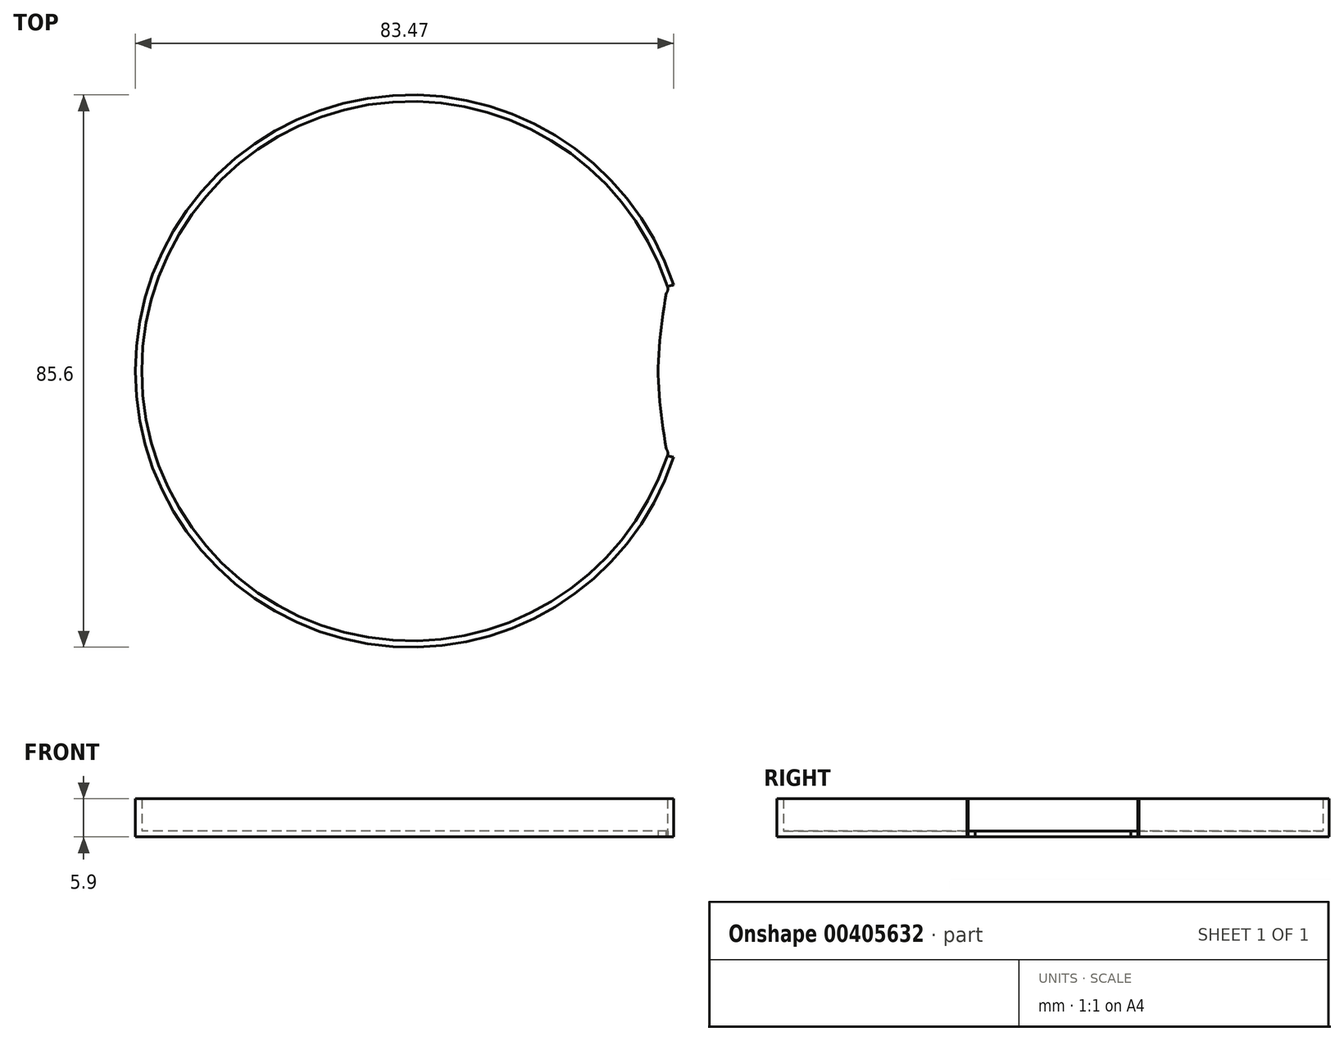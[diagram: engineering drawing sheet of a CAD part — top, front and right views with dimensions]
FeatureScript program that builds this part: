
annotation { "Feature Type Name" : "Feature", "Feature Type Description" : "" }
export const myFeature = defineFeature(function(context is Context, id is Id, definition is map)
    precondition{}
    {
        {
            var Q0;
            Q0=qCreatedBy(makeId("Top.planeOp"),FACE);
            var sketch = newSketch(context, id + "F0", { "sketchPlane" : qUnion([Q0])});
            skCircle(sketch, "E0", {"center": v(0, 0) * mm, "radius": 42.8 * mm});
            skCircle(sketch, "E1", {"center": v(42.8, 0) * mm, "radius": 13.5 * mm});
            skCircle(sketch, "E2.0", {"center": v(0, 0) * mm, "radius": 41.8 * mm});
            skCircle(sketch, "E3.0", {"center": v(42.8, 0) * mm, "radius": 12.5 * mm});
            skFitSpline(sketch, "E4", {"points": [v(39.68, -13.14) * mm, v(38.27, 0) * mm, v(39.68, 13.14) * mm], "startDerivative": vector(-4.24, 26.27) * mm, "endDerivative": vector(4.24, 26.27) * mm});
            skSolve(sketch);
        }
        {
            var Q0;
            {var subQ0=sQuery(id+"F0.wireOp",EDGE,"E2.0");var subQ1=sQuery(id+"F0.wireOp",EDGE,"E1");var subQ2=makeQuery(id+"F0.imprint","INTERSECT",VERTEX,{"disambiguationData":[OD(0.0)],"derivedFrom":[subQ1,subQ0]});Q0=makeQuery(id+"F0.imprint","IMPRINT",FACE,{"disambiguationData":[TD([[makeQuery(id+"F0.imprint","IMPRINT",EDGE,{"disambiguationData":[TD([[subQ2,-1.0]])],"derivedFrom":subQ1}),-1.0]])]});}
            var Q1;
            {var subQ0=sQuery(id+"F0.wireOp",EDGE,"E1");var subQ1=sQuery(id+"F0.wireOp",EDGE,"E0");var subQ2=makeQuery(id+"F0.imprint","INTERSECT",VERTEX,{"disambiguationData":[OD(0.0)],"derivedFrom":[subQ1,subQ0]});Q1=makeQuery(id+"F0.imprint","IMPRINT",FACE,{"disambiguationData":[TD([[makeQuery(id+"F0.imprint","IMPRINT",EDGE,{"disambiguationData":[TD([[subQ2,-1.0]])],"derivedFrom":subQ1}),1.0]])]});}
            var Q2;
            {var subQ0=sQuery(id+"F0.wireOp",EDGE,"E4");var subQ1=sQuery(id+"F0.wireOp",EDGE,"E2.0");var subQ2=sQuery(id+"F0.wireOp",EDGE,"E1");var subQ3=makeQuery(id+"F0.imprint","INTERSECT",VERTEX,{"disambiguationData":[OD(0.0)],"derivedFrom":[subQ2,subQ1,subQ0]});Q2=makeQuery(id+"F0.imprint","IMPRINT",FACE,{"disambiguationData":[TD([[makeQuery(id+"F0.imprint","IMPRINT",EDGE,{"disambiguationData":[TD([[subQ3,1.0]])],"derivedFrom":subQ2}),-1.0]])]});}
            var Q3;
            {var subQ0=sQuery(id+"F0.wireOp",EDGE,"E4");var subQ1=sQuery(id+"F0.wireOp",EDGE,"E3.0");var subQ2=makeQuery(id+"F0.imprint","INTERSECT",VERTEX,{"disambiguationData":[OD(0.0)],"derivedFrom":[subQ1,subQ0]});Q3=makeQuery(id+"F0.imprint","IMPRINT",FACE,{"disambiguationData":[TD([[makeQuery(id+"F0.imprint","IMPRINT",EDGE,{"disambiguationData":[TD([[subQ2,-1.0]])],"derivedFrom":subQ1}),1.0]])]});}
            var Q4;
            {var subQ0=sQuery(id+"F0.wireOp",EDGE,"E4");var subQ5=sQuery(id+"F0.wireOp",EDGE,"E3.0");var subQ6=makeQuery(id+"F0.imprint","INTERSECT",VERTEX,{"disambiguationData":[OD(0.0)],"derivedFrom":[subQ5,subQ0]});Q4=makeQuery(id+"F0.imprint","IMPRINT",FACE,{"disambiguationData":[TD([[makeQuery(id+"F0.imprint","IMPRINT",EDGE,{"disambiguationData":[TD([[subQ6,-1.0]])],"derivedFrom":subQ5}),-1.0]])]});}
            var Q5;
            {var subQ1=sQuery(id+"F0.wireOp",EDGE,"E2.0");var subQ3=sQuery(id+"F0.wireOp",EDGE,"E3.0");var subQ4=makeQuery(id+"F0.imprint","INTERSECT",VERTEX,{"disambiguationData":[OD(0.0)],"derivedFrom":[subQ1,subQ3]});Q5=makeQuery(id+"F0.imprint","IMPRINT",FACE,{"disambiguationData":[TD([[makeQuery(id+"F0.imprint","IMPRINT",EDGE,{"disambiguationData":[TD([[subQ4,-1.0]])],"derivedFrom":subQ3}),-1.0]])]});}
            var Q6;
            {var subQ1=sQuery(id+"F0.wireOp",EDGE,"E2.0");var subQ3=sQuery(id+"F0.wireOp",EDGE,"E3.0");var subQ4=makeQuery(id+"F0.imprint","INTERSECT",VERTEX,{"disambiguationData":[OD(1.0)],"derivedFrom":[subQ1,subQ3]});Q6=makeQuery(id+"F0.imprint","IMPRINT",FACE,{"disambiguationData":[TD([[makeQuery(id+"F0.imprint","IMPRINT",EDGE,{"disambiguationData":[TD([[subQ4,1.0]])],"derivedFrom":subQ3}),-1.0]])]});}
            extrude(context, id + "F1", {"entities" : qUnion([Q0, Q1, Q2, Q3, Q4, Q5, Q6]), "oppositeDirection" : true, "depth" : 0.9 * mm});
        }
        {
            var Q0;
            {var subQ0=sQuery(id+"F0.wireOp",EDGE,"E1");var subQ1=sQuery(id+"F0.wireOp",EDGE,"E0");var subQ2=makeQuery(id+"F0.imprint","INTERSECT",VERTEX,{"disambiguationData":[OD(0.0)],"derivedFrom":[subQ1,subQ0]});Q0=makeQuery(id+"F0.imprint","IMPRINT",FACE,{"disambiguationData":[TD([[makeQuery(id+"F0.imprint","IMPRINT",EDGE,{"disambiguationData":[TD([[subQ2,-1.0]])],"derivedFrom":subQ1}),1.0]])]});}
            extrude(context, id + "F2", {"entities" : qUnion([Q0]), "operationType" : NewBodyOperationType.ADD, "depth" : 5 * mm});
        }
        {
            var Q0;
            {var subQ0=sQuery(id+"F0.wireOp",EDGE,"E3.0");var subQ1=sQuery(id+"F0.wireOp",EDGE,"E2.0");Q0=makeQuery(id+"F1.opExtrude","SWEPT_EDGE",EDGE,{"disambiguationData":[OSD([subQ1,subQ0]),TDD([makeQuery(id+"F0.imprint","INTERSECT",VERTEX,{"disambiguationData":[OD(1.0)],"derivedFrom":[subQ1,subQ0]})])]});}
            var Q1;
            {var subQ0=sQuery(id+"F0.wireOp",EDGE,"E3.0");var subQ1=sQuery(id+"F0.wireOp",EDGE,"E2.0");Q1=makeQuery(id+"F1.opExtrude","SWEPT_EDGE",EDGE,{"disambiguationData":[OSD([subQ1,subQ0]),TDD([makeQuery(id+"F0.imprint","INTERSECT",VERTEX,{"disambiguationData":[OD(0.0)],"derivedFrom":[subQ1,subQ0]})])]});}
            fillet(context, id + "F3", {"entities" : qUnion([Q0, Q1]), "radius" : 1 * mm, "tangentPropagation" : true, "allowEdgeOverflow" : false});
        }
    });
